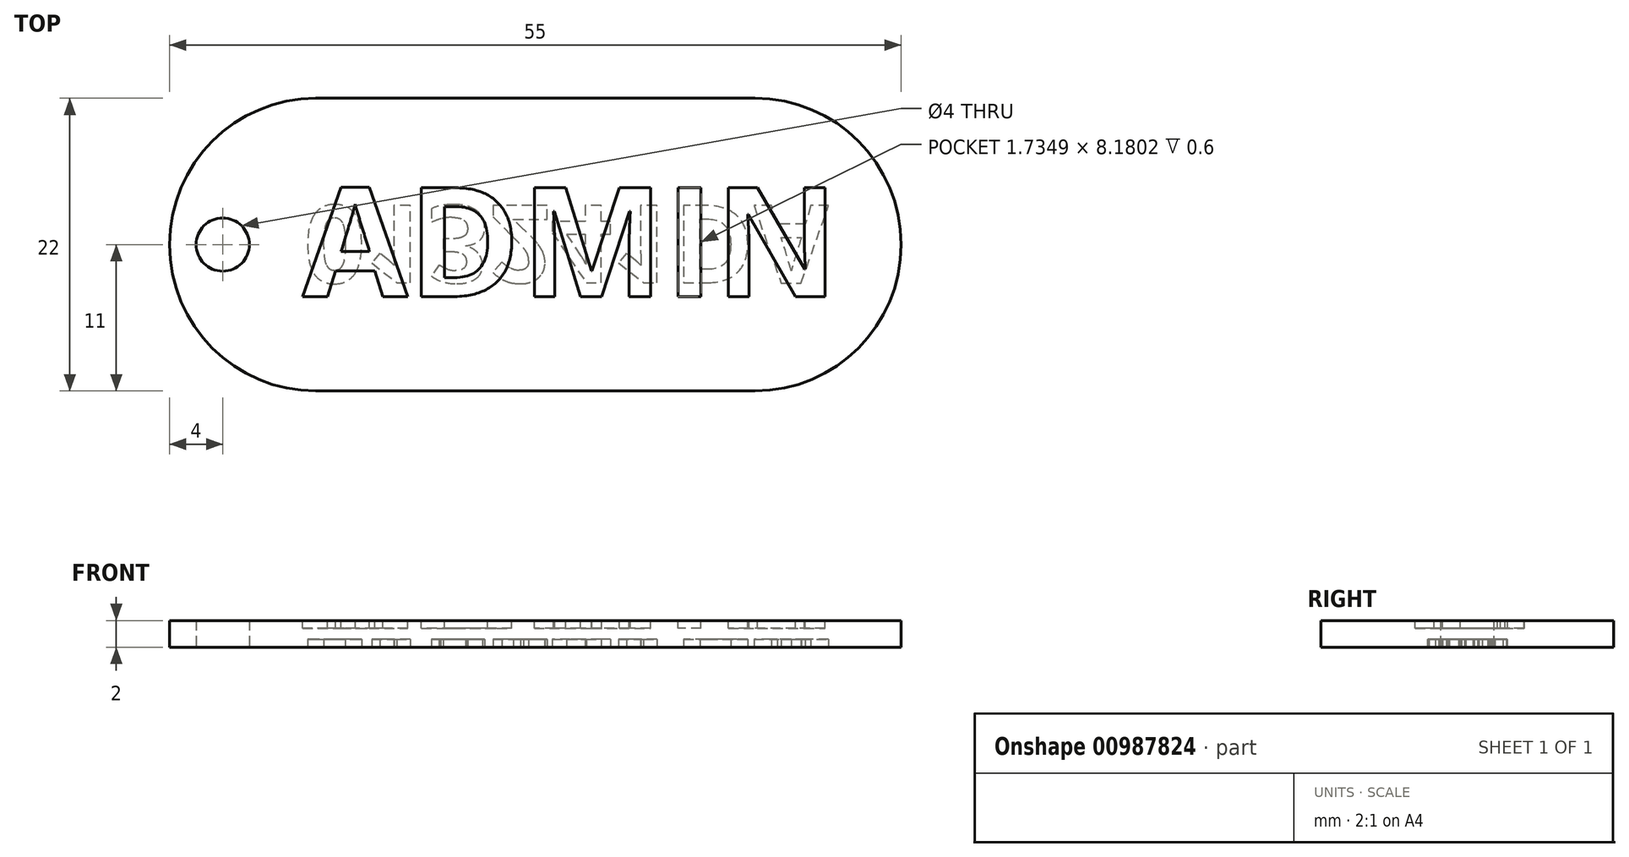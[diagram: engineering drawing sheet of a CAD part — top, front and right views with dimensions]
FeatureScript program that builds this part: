
annotation { "Feature Type Name" : "Feature", "Feature Type Description" : "" }
export const myFeature = defineFeature(function(context is Context, id is Id, definition is map)
    precondition{}
    {
        {
            var Q0;
            Q0=qCreatedBy(makeId("Top.planeOp"),FACE);
            var sketch = newSketch(context, id + "F0", { "sketchPlane" : qUnion([Q0])});
            skLineSegment(sketch, "E0.bottom", {"start": v(16.5, -11) * mm, "end": v(-16.5, -11) * mm});
            skLineSegment(sketch, "E0.top", {"start": v(16.5, 11) * mm, "end": v(-16.5, 11) * mm});
            skLineSegment(sketch, "E0.left", {"start": v(16.5, -11) * mm, "end": v(16.5, 11) * mm});
            skLineSegment(sketch, "E0.right", {"start": v(-16.5, -11) * mm, "end": v(-16.5, 11) * mm});
            skPoint(sketch, "E0.middle", {"position": v(0, 0) * mm});
            skCircle(sketch, "E1", {"center": v(-16.5, 0) * mm, "radius": 11 * mm});
            skCircle(sketch, "E2", {"center": v(16.5, 0) * mm, "radius": 11 * mm});
            skPoint(sketch, "E3", {"position": v(-23.5, 0) * mm});
            skSolve(sketch);
        }
        {
            var Q0;
            {var subQ0=sQuery(id+"F0.wireOp",EDGE,"E0.right");Q0=makeQuery(id+"F0.imprint","IMPRINT",FACE,{"disambiguationData":[TD([[makeQuery(id+"F0.imprint","IMPRINT",EDGE,{"derivedFrom":subQ0}),-1.0]])]});}
            var Q1;
            {var subQ0=sQuery(id+"F0.wireOp",EDGE,"E0.right");Q1=makeQuery(id+"F0.imprint","IMPRINT",FACE,{"disambiguationData":[TD([[makeQuery(id+"F0.imprint","IMPRINT",EDGE,{"derivedFrom":subQ0}),1.0]])]});}
            var Q2;
            {var subQ0=sQuery(id+"F0.wireOp",EDGE,"E0.left");Q2=makeQuery(id+"F0.imprint","IMPRINT",FACE,{"disambiguationData":[TD([[makeQuery(id+"F0.imprint","IMPRINT",EDGE,{"derivedFrom":subQ0}),1.0]])]});}
            var Q3;
            {var subQ0=sQuery(id+"F0.wireOp",EDGE,"E0.bottom");Q3=makeQuery(id+"F0.imprint","IMPRINT",FACE,{"disambiguationData":[TD([[makeQuery(id+"F0.imprint","IMPRINT",EDGE,{"derivedFrom":subQ0}),-1.0]])]});}
            var Q4;
            {var subQ0=sQuery(id+"F0.wireOp",EDGE,"E0.left");Q4=makeQuery(id+"F0.imprint","IMPRINT",FACE,{"disambiguationData":[TD([[makeQuery(id+"F0.imprint","IMPRINT",EDGE,{"derivedFrom":subQ0}),-1.0]])]});}
            extrude(context, id + "F1", {"entities" : qUnion([Q0, Q1, Q2, Q3, Q4]), "depth" : 2 * mm, "offsetDistance" : 25 * mm});
        }
        {
            var Q0;
            Q0=sQuery(id+"F0.wireOp",VERTEX,"E3");
            var Q1;
            Q1=makeQuery(id+"F1.opExtrude","SWEPT_BODY",BODY,{"disambiguationData":[OSD([sQuery(id+"F0.wireOp",EDGE,"E0.bottom"),sQuery(id+"F0.wireOp",EDGE,"E0.top"),sQuery(id+"F0.wireOp",EDGE,"E1"),sQuery(id+"F0.wireOp",EDGE,"E2")])]});
            hole(context, id + "F2", {"style" : HoleStyle.SIMPLE, "endStyle" : HoleEndStyle.THROUGH, "oppositeDirection" : true, "holeDiameter" : 4 * mm, "majorDiameter" : 5 * mm, "isTappedThrough" : true, "tappedDepth" : 12 * mm, "tapClearance" : 3, "locations" : qUnion([Q0]), "scope" : qUnion([Q1])});
        }
        {
            var Q0;
            Q0=makeQuery(id+"F1.opExtrude","CAP_FACE",FACE,{"disambiguationData":[OSD([sQuery(id+"F0.wireOp",EDGE,"E0.bottom"),sQuery(id+"F0.wireOp",EDGE,"E0.top"),sQuery(id+"F0.wireOp",EDGE,"E1"),sQuery(id+"F0.wireOp",EDGE,"E2")])],"isStart":false});
            var sketch = newSketch(context, id + "F3", { "sketchPlane" : qUnion([Q0])});
            skText(sketch, "E4", { "text": "ADMIN", "fontName": "OpenSans-Bold.ttf"});
            const initialGuessF3  = {"E4": [-0.0175, -0.00391, 1, 0, 0.00825]};
            skSetInitialGuess(sketch, initialGuessF3);
            skSolve(sketch);
        }
        {
            var Q0;
            Q0 = qSketchRegion(id + "F3", true);
            extrude(context, id + "F4", {"entities" : qUnion([Q0]), "operationType" : NewBodyOperationType.REMOVE, "oppositeDirection" : true, "depth" : 0.6 * mm, "offsetDistance" : 25 * mm});
        }
        {
            var Q0;
            Q0=makeQuery(id+"F1.opExtrude","CAP_FACE",FACE,{"disambiguationData":[OSD([sQuery(id+"F0.wireOp",EDGE,"E0.bottom"),sQuery(id+"F0.wireOp",EDGE,"E0.top"),sQuery(id+"F0.wireOp",EDGE,"E1"),sQuery(id+"F0.wireOp",EDGE,"E2")])],"isStart":true});
            var sketch = newSketch(context, id + "F5", { "sketchPlane" : qUnion([Q0])});
            skText(sketch, "E5", { "text": "013241DA", "fontName": "OpenSans-Bold.ttf"});
            const initialGuessF5  = {"E5": [-0.01741, -0.00294, 1, 0, 0.00585]};
            skSetInitialGuess(sketch, initialGuessF5);
            skSolve(sketch);
        }
        {
            var Q0;
            Q0 = qSketchRegion(id + "F5", true);
            extrude(context, id + "F6", {"entities" : qUnion([Q0]), "operationType" : NewBodyOperationType.REMOVE, "oppositeDirection" : true, "depth" : 0.6 * mm, "offsetDistance" : 25 * mm});
        }
    });
